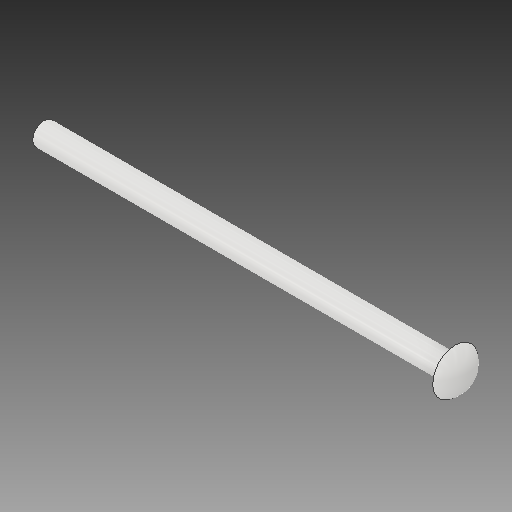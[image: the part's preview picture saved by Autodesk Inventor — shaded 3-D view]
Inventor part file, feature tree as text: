
AUTODESK INVENTOR PART (.ipt)
format: ipt  version: 2020 (Build 240168000, 168)  size: 107,008 bytes
history: native  units: in
note: dims shown in document units (in); Inventor stores cm internally (conversion verified against a paired STEP export)
features: revolve x1, sketch x1
ambient origin geometry x8: Origin, YZ Plane, XZ Plane, XY Plane, X Axis, Y Axis, Z Axis, Center Point
bodies: Solid1 (feature_tree)
feature tree (2):
  revolve  "Revolution1"  [1 undecoded]
  sketch  "Sketch1"  dims[d0=4.0in d1=0.4375in d2=0.125in d3=0.2188in d4=90.0deg]
note: 1 required parameter value undecoded (feature->parameter linkage not recoverable at this tier; creation-order binding heuristic only, values carry confidence <= 0.55)
